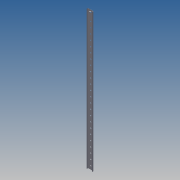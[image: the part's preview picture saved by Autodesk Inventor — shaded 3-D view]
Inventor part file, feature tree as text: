
AUTODESK INVENTOR PART (.ipt)
format: ipt  version: 2011 (Build 150239000, 239)  size: 248,832 bytes
history: native  units: mm
features: fillet x6, extrude x4, sketch x4
ambient origin geometry x8: Origin, YZ Plane, XZ Plane, XY Plane, X Axis, Y Axis, Z Axis, Center Point
feature tree (14):
  extrude  "Extrusion10"  Depth=510.0mm TaperAngle=0.0deg
  extrude  "Extrusion11"  Depth=1.0mm
  extrude  "Extrusion12"  Depth=5.0mm
  fillet  "Fillet12"  Radius=6.799998mm
  fillet  "Fillet13"  Radius=5.0mm
  fillet  "Fillet14"  Radius=6.799998mm
  fillet  "Fillet15"  Radius=4.5mm
  fillet  "Fillet16"  Radius=0.3mm
  fillet  "Fillet17"  Radius=0.3mm
  extrude  "Extrusion13"  Depth=0.1mm
  sketch  "Sketch1"  dims[d105=0.1mm d106=510.0mm d107=0.0mm]
  sketch  "Sketch12"  dims[d108=5.3mm d109=1.0mm]
  sketch  "Sketch13"  dims[d110=0.3mm d111=0.0mm d112=5.0mm d113=6.799998mm d115=5.0mm d116=6.799998mm d117=4.5mm d118=0.0mm d119=0.3mm d120=0.3mm]
  sketch  "Sketch14"  dims[d121=0.1mm d122=0.1mm d123=1.0mm d124=1.0mm d137=20.0mm d138=20.0mm d143=12.4mm d144=20.0mm d145=20.0mm d146=20.0mm d147=20.0mm d148=20.0mm d149=20.0mm d150=9.299998mm d151=9.299998mm d152=9.299998mm d153=9.299998mm d154=9.299998mm d155=9.299998mm d156=9.3mm d157=9.3mm d158=9.3mm d159=9.3mm d160=9.3mm d161=9.3mm d162=9.3mm d163=9.3mm d164=9.3mm d165=20.0mm d166=20.0mm d167=20.0mm d168=20.0mm d169=20.0mm d170=20.0mm d171=20.0mm d172=20.0mm d173=20.0mm d174=20.0mm d175=20.0mm d176=20.0mm d177=9.3mm d178=9.300002mm d179=9.3mm d180=9.3mm d181=20.0mm d182=20.0mm d183=9.3mm d184=20.0mm d185=2.0mm d186=0.0mm]
